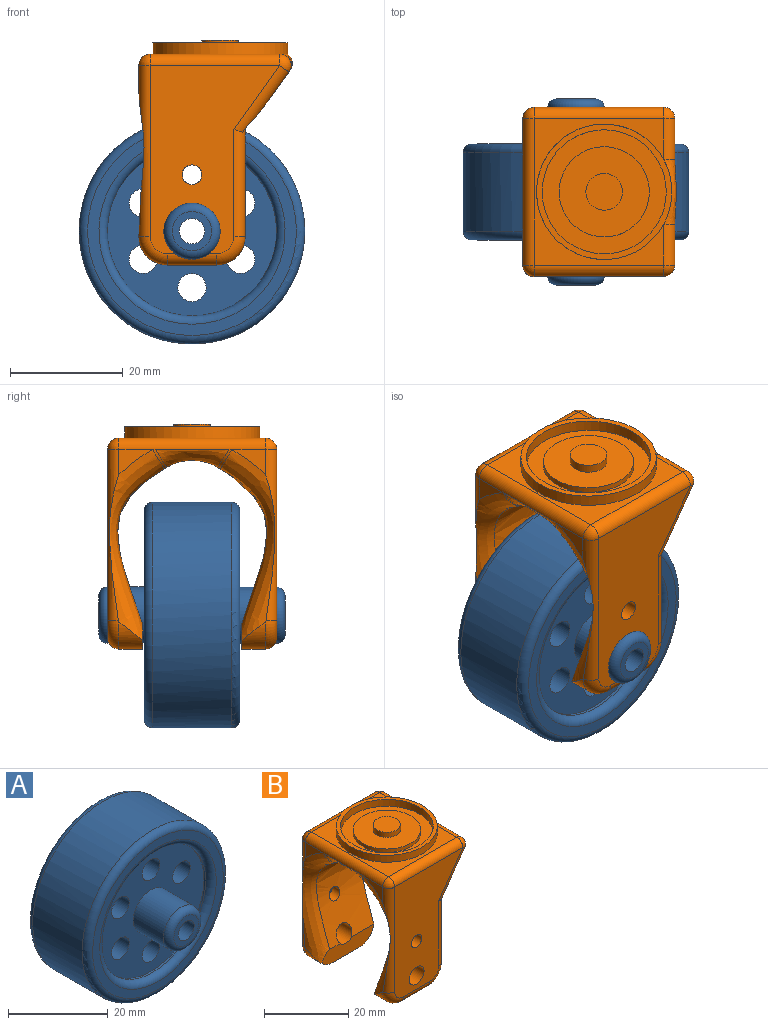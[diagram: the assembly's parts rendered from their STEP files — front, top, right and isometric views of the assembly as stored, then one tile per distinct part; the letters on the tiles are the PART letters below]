
ASSEMBLY  parts=2 mates=1
PART A: 24 faces, bbox 43.3x33x43.3 mm
  f0: cylinder r=15mm len=30mm, axis (0,1,0), area 47.1mm2, adj f9,f20
  f1: cylinder r=20mm len=40mm, axis (0,1,0), area 1759.3mm2, adj f19,f21
  f2: plane 37x37mm, normal (0,-1,0), area 219.9mm2, adj f20,f21
  f3: cylinder r=2.5mm len=13mm, axis (0,1,0), area 204.2mm2, adj f9,f15
  f4: cylinder r=2.5mm len=13mm, axis (0,1,0), area 204.2mm2, adj f9,f15
  f5: cylinder r=2.5mm len=13mm, axis (0,1,0), area 204.2mm2, adj f9,f15
  f6: cylinder r=2.5mm len=13mm, axis (0,1,0), area 204.2mm2, adj f9,f15
  f7: cylinder r=2.5mm len=13mm, axis (0,1,0), area 204.2mm2, adj f9,f15
  f8: cylinder r=2.5mm len=13mm, axis (0,1,0), area 204.2mm2, adj f9,f15
  f9: plane 30x30mm, normal (0,-1,0), area 510.5mm2, adj f0,f3,f4,f5,f6,f7,f8,f11
  f10: cylinder r=2.25mm len=33mm, axis (0,1,0), area 466.5mm2, adj f12,f17
  f11: cylinder r=5mm len=10mm, axis (0,1,0), area 267mm2, adj f9,f23
  f12: plane 7x7mm, normal (0,-1,0), area 22.6mm2, adj f10,f23
  f13: cylinder r=15mm len=30mm, axis (0,-1,0), area 47.1mm2, adj f15,f18
  f14: plane 37x37mm, normal (0,1,0), area 219.9mm2, adj f18,f19
  f15: plane 30x30mm, normal (0,1,0), area 510.5mm2, adj f3,f4,f5,f6,f7,f8,f13,f16
  f16: cylinder r=5mm len=10mm, axis (0,-1,0), area 267mm2, adj f15,f22
  f17: plane 7x7mm, normal (0,1,0), area 22.6mm2, adj f10,f22
  f18: torus R=16.5mm, axis (0,1,0), area 230.1mm2, adj f13,f14
  f19: torus R=18.5mm, axis (0,1,0), area 288mm2, adj f1,f14
  f20: torus R=16.5mm, axis (0,-1,0), area 230.1mm2, adj f0,f2
  f21: torus R=18.5mm, axis (0,-1,0), area 288mm2, adj f1,f2
  f22: torus R=3.5mm, axis (0,1,0), area 66mm2, adj f16,f17
  f23: torus R=3.5mm, axis (0,-1,0), area 66mm2, adj f11,f12
PART B: 64 faces, bbox 29.8x34.5x72.5 mm
  f0: plane 5.99x4.51mm, normal (-1,0,0), area 12.2mm2, adj f37,f41,f61
  f1: plane 8.44x5.73mm, normal (0.81,0,-0.58), area 25.1mm2, adj f35,f40,f43,f55,f56
  f2: plane 4.71x2.57mm, normal (1,0,0), area 1.2mm2, adj f13,f33,f56
  f3: plane 13.35x4.27mm, normal (1,0,0), area 23.7mm2, adj f12,f23,f52
  f4: plane 4.71x2.57mm, normal (1,0,0), area 1.2mm2, adj f12,f52,f54
  f5: plane 13.35x4.27mm, normal (1,0,0), area 23.7mm2, adj f13,f21,f33
  f6: plane 8.84x4.23mm, normal (0,0,-1), area 37.4mm2, adj f14,f23,f24,f48
  f7: plane 8.84x4.23mm, normal (0,0,-1), area 37.4mm2, adj f15,f21,f22,f32
  f8: plane 26x22.95mm, normal (0,0,1), area 155.7mm2, adj f26,f36,f40,f41,f46,f47
  f9: plane 5.99x4.51mm, normal (-1,0,0), area 12.2mm2, adj f41,f42,f57
  f10: plane 33.39x22.95mm, normal (0,1,0), area 508.3mm2, adj f17,f19,f42,f45,f47,f48,f50,f51
  f11: plane 33.39x22.95mm, normal (0,-1,0), area 508.3mm2, adj f16,f18,f31,f32,f33,f34,f35,f36
  f12: extruded ~27.88x18.71mm, area 465.6mm2, adj f3,f4,f14,f17,f19,f23,f52,f53
  f13: extruded ~27.88x18.71mm, area 465.6mm2, adj f2,f5,f15,f16,f18,f21,f33,f53
  f14: plane 17.34x4.34mm, normal (0,-1,0), area 64mm2, adj f6,f12,f17,f23,f24,f57
  f15: plane 17.34x4.34mm, normal (0,1,0), area 64mm2, adj f7,f13,f16,f21,f22,f61
  f16: cylinder r=2.5mm len=6.23mm, axis (0,-1,0), area 88mm2, adj f11,f13,f15
  f17: cylinder r=2.5mm len=6.23mm, axis (0,-1,0), area 88mm2, adj f10,f12,f14
  f18: cylinder r=1.75mm len=3.5mm, axis (0,-1,0), area 31.6mm2, adj f11,f13
  f19: cylinder r=1.75mm len=3.5mm, axis (0,-1,0), area 31.6mm2, adj f10,f12
  f20: plane 8.44x5.73mm, normal (0.81,0,-0.58), area 25.1mm2, adj f43,f46,f51,f54,f55
  f21: cylinder r=5mm len=5mm, axis (0,1,0), area 33.2mm2, adj f5,f7,f13,f15,f31
  f22: cylinder r=5mm len=5mm, axis (0,-1,0), area 24.6mm2, adj f7,f15,f34,f61
  f23: cylinder r=5mm len=5mm, axis (0,1,0), area 33.2mm2, adj f3,f6,f12,f14,f50
  f24: cylinder r=5mm len=5mm, axis (0,-1,0), area 24.6mm2, adj f6,f14,f45,f57
  f25: cylinder r=11mm len=22mm, axis (0,0,-1), area 138.2mm2, adj f27,f28
  f26: cylinder r=12mm len=24mm, axis (0,0,-1), area 150.8mm2, adj f8,f27,f43
  f27: plane 24x24mm, normal (0,0,1), area 72.3mm2, adj f25,f26
  f28: plane 22x22mm, normal (0,0,1), area 179.1mm2, adj f25,f29
  f29: cylinder r=8mm len=16mm, axis (0,0,-1), area 50.3mm2, adj f28,f30
  f30: plane 16x16mm, normal (0,0,1), area 167.9mm2, adj f29,f62
  f31: torus R=3mm, axis (0,-1,0), area 21.1mm2, adj f11,f21,f32,f33
  f32: cylinder r=2mm len=8.84mm, axis (1,0,0), area 27.8mm2, adj f7,f11,f31,f34
  f33: cylinder r=2mm len=20.12mm, axis (0,0,1), area 59.1mm2, adj f2,f5,f11,f13,f31,f35,f56
  f34: torus R=3mm, axis (0,-1,0), area 21.1mm2, adj f11,f22,f32,f37,f61
  f35: cylinder r=2mm len=12.52mm, axis (0.58,0,0.81), area 37.9mm2, adj f1,f11,f33,f38,f56
  f36: cylinder r=2mm len=22.95mm, axis (-1,0,0), area 72.1mm2, adj f8,f11,f38,f39
  f37: cylinder r=2mm len=30.39mm, axis (0,0,-1), area 64mm2, adj f0,f11,f34,f39,f61
  f38: sphere r=2mm, area 8.2mm2, adj f35,f36,f40
  f39: sphere r=2mm, area 6.3mm2, adj f36,f37,f41
  f40: cylinder r=2mm len=7.25mm, axis (0,1,0), area 31.8mm2, adj f1,f8,f38,f43
  f41: cylinder r=2mm len=26mm, axis (0,1,0), area 81.7mm2, adj f0,f8,f9,f39,f44,f58,f59,f60
  f42: cylinder r=2mm len=30.39mm, axis (0,0,1), area 64mm2, adj f9,f10,f44,f45,f57
  f43: bspline ~12.2x4.38mm, area 40.5mm2, adj f1,f20,f26,f40,f46,f55
  f44: sphere r=2mm, area 8.6mm2, adj f41,f42,f47
  f45: torus R=3mm, axis (0,-1,0), area 21.1mm2, adj f10,f24,f42,f48,f57
  f46: cylinder r=2mm len=7.25mm, axis (0,1,0), area 31.8mm2, adj f8,f20,f43,f49
  f47: cylinder r=2mm len=22.95mm, axis (1,0,0), area 72.1mm2, adj f8,f10,f44,f49
  f48: cylinder r=2mm len=8.84mm, axis (-1,0,0), area 27.8mm2, adj f6,f10,f45,f50
  f49: sphere r=2mm, area 5.9mm2, adj f46,f47,f51
  f50: torus R=3mm, axis (0,-1,0), area 21.1mm2, adj f10,f23,f48,f52
  f51: cylinder r=2mm len=12.52mm, axis (0.58,0,0.81), area 37.9mm2, adj f10,f20,f49,f52,f54
  f52: cylinder r=2mm len=20.12mm, axis (0,0,-1), area 59.1mm2, adj f3,f4,f10,f12,f50,f51,f54
  f53: cylinder r=9mm len=18.71mm, axis (1,0,0), area 177mm2, adj f12,f13,f55,f59
  f54: bspline ~14.76x12.67mm, area 51.1mm2, adj f4,f12,f20,f51,f52,f55
  f55: bspline ~13.04x4.51mm, area 46.1mm2, adj f1,f20,f43,f53,f54,f56
  f56: bspline ~14.76x12.67mm, area 51.1mm2, adj f1,f2,f13,f33,f35,f55
  f57: bspline ~68.98x20.51mm, area 169.9mm2, adj f9,f12,f14,f24,f42,f45,f58
  f58: bspline ~4.61x4.34mm, area 2.8mm2, adj f12,f41,f57,f59
  f59: bspline ~14.52x4.19mm, area 50.5mm2, adj f41,f53,f58,f60
  f60: bspline ~4.61x4.34mm, area 2.8mm2, adj f13,f41,f59,f61
  f61: bspline ~68.98x20.51mm, area 169.9mm2, adj f0,f13,f15,f22,f34,f37,f60
  f62: cylinder r=3.25mm len=6.5mm, axis (0,0,-1), area 30.6mm2, adj f30,f63
  f63: plane 6.5x6.5mm, normal (0,0,1), area 33.2mm2, adj f62
PLACE A t=(-12.48,20.76,11.71)mm
PLACE B t=(-3.06,-2.77,5.71)mm
MATE revolute A.f11 <-> B.f16  axis (0,-1,0) through (-12.48,5.76,11.71)mm
